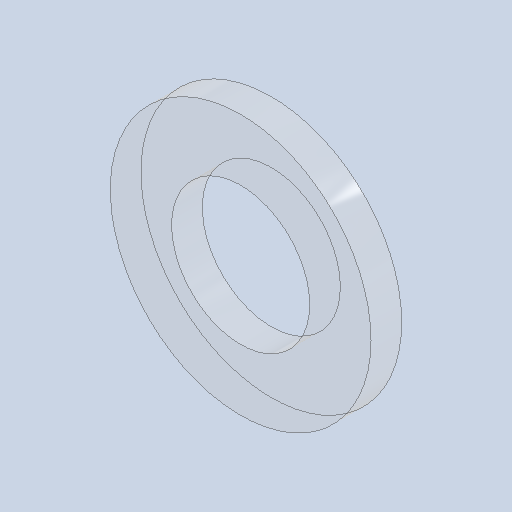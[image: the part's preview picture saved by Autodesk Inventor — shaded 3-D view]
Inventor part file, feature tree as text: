
AUTODESK INVENTOR PART (.ipt)
format: ipt  version: 2022 (Build 260153000, 153)  size: 106,496 bytes
history: native  units: mm
features: extrude x1, sketch x1
ambient origin geometry x8: Origin, YZ Plane, XZ Plane, XY Plane, X Axis, Y Axis, Z Axis, Center Point
bodies: Solid1 (feature_tree)
feature tree (2):
  extrude  "Extrusion1"  Depth=2.0mm
  sketch  "Sketch1"  dims[d0=17.0mm d1=9.0mm d2=2.0mm d3=0.0mm]
